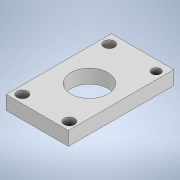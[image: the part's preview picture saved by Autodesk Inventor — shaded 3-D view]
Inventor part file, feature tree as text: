
AUTODESK INVENTOR PART (.ipt)
format: ipt  version: 2020 (Build 240168000, 168)  size: 112,128 bytes
history: native  units: mm
features: extrude x1, sketch x1
ambient origin geometry x8: Origin, YZ Plane, XZ Plane, XY Plane, X Axis, Y Axis, Z Axis, Center Point
bodies: Body1 (feature_tree)
feature tree (2):
  extrude  "Extrusion2"  Depth=5.0mm
  sketch  "Sketch2"  dims[d2=5.0mm d3=0.0mm d0=0.5mm d1=0.872665mm]
